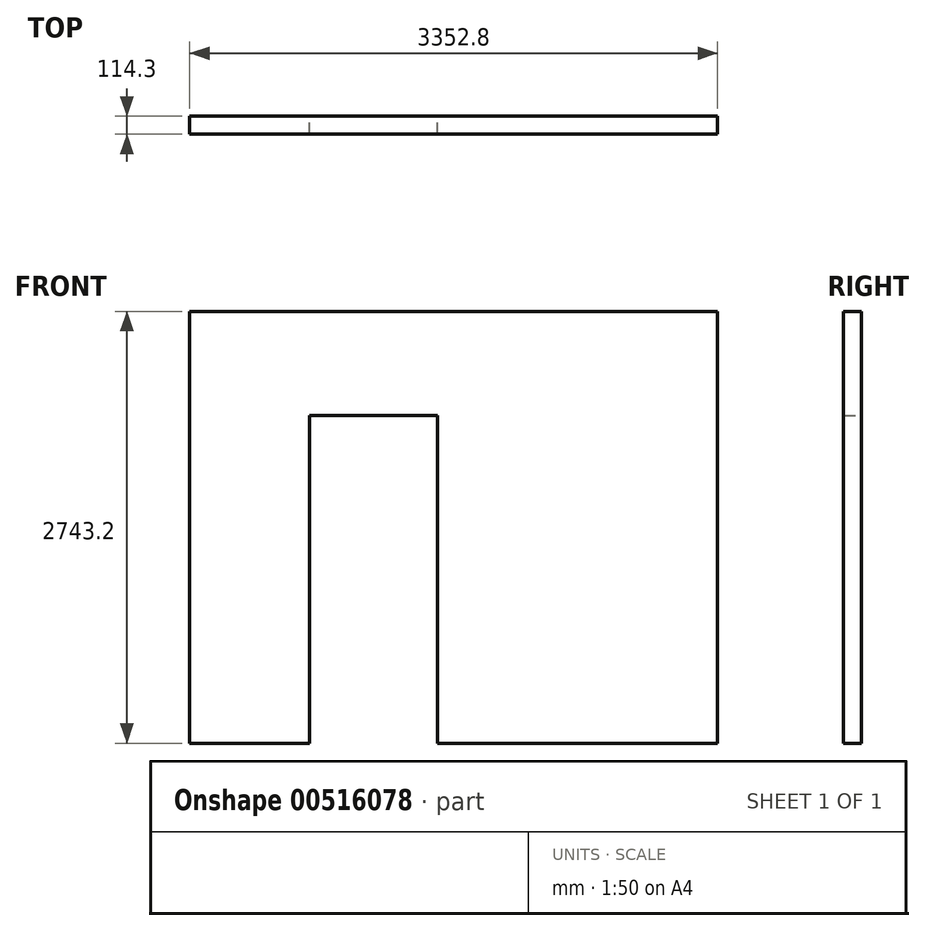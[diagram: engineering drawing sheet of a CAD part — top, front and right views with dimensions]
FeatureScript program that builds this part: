
annotation { "Feature Type Name" : "Feature", "Feature Type Description" : "" }
export const myFeature = defineFeature(function(context is Context, id is Id, definition is map)
    precondition{}
    {
        {
            var Q0;
            Q0=qCreatedBy(makeId("Front.planeOp"),FACE);
            var sketch = newSketch(context, id + "F0", { "sketchPlane" : qUnion([Q0])});
            skLineSegment(sketch, "E0.bottom", {"start": v(1778, -1371.6) * mm, "end": v(-1574.8, -1371.6) * mm});
            skLineSegment(sketch, "E0.top", {"start": v(1778, 1371.6) * mm, "end": v(-1574.8, 1371.6) * mm});
            skLineSegment(sketch, "E0.left", {"start": v(1778, -1371.6) * mm, "end": v(1778, 1371.6) * mm});
            skLineSegment(sketch, "E0.right", {"start": v(-1574.8, -1371.6) * mm, "end": v(-1574.8, 1371.6) * mm});
            skPoint(sketch, "E0.middle", {"position": v(101.6, 0) * mm});
            skLineSegment(sketch, "E1.bottom", {"start": v(-812.8, -1371.6) * mm, "end": v(0, -1371.6) * mm});
            skLineSegment(sketch, "E1.top", {"start": v(-812.8, 711.2) * mm, "end": v(0, 711.2) * mm});
            skLineSegment(sketch, "E1.left", {"start": v(-812.8, -1371.6) * mm, "end": v(-812.8, 711.2) * mm});
            skLineSegment(sketch, "E1.right", {"start": v(0, -1371.6) * mm, "end": v(0, 711.2) * mm});
            skSolve(sketch);
        }
        {
            var Q0;
            Q0=makeQuery(id+"F0.imprint","IMPRINT",FACE,{"disambiguationData":[TD([[makeQuery(id+"F0.imprint","IMPRINT",EDGE,{"derivedFrom":sQuery(id+"F0.wireOp",EDGE,"E0.bottom")}),-1.0]])]});
            extrude(context, id + "F1", {"entities" : qUnion([Q0]), "depth" : 114.3 * mm, "offsetDistance" : 25.4 * mm});
        }
    });
